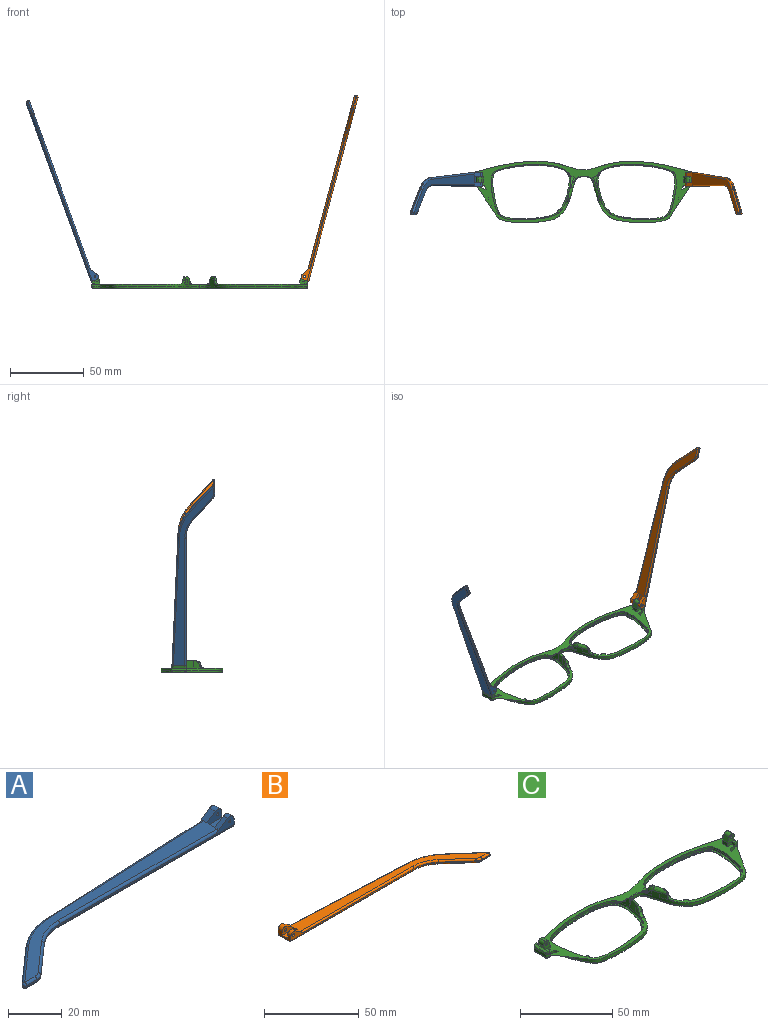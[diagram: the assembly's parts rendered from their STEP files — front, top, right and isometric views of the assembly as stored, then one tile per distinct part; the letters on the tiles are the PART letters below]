
ASSEMBLY  parts=3 mates=2
PART A: 43 faces, bbox 130.2x29.5x5.9 mm
  f0: plane 9.62x3.72mm, normal (1,0,0), area 24.7mm2, adj f1,f3,f4,f5,f10,f16,f18,f28
  f1: cylinder r=2.2mm len=3.45mm, axis (0,-1,0), area 11mm2, adj f0,f2,f4,f37
  f2: plane 6.01x3.91mm, normal (-0.55,0,0.84), area 12.7mm2, adj f1,f4,f9,f19,f37
  f3: plane 2.26x0.1mm, normal (0,0,1), area 0.1mm2, adj f0,f5,f18
  f4: plane 92.1x4.9mm, normal (0,-1,0), area 79.9mm2, adj f0,f1,f2,f14,f19,f36,f42
  f5: plane 93.42x4.13mm, normal (-0.04,1,0), area 64.8mm2, adj f0,f3,f11,f15,f17,f27,f28
  f6: plane 17.82x15.72mm, normal (-0.66,0.75,0), area 14.3mm2, adj f11,f12,f25,f30
  f7: plane 5.46x0.6mm, normal (0,-1,0), area 3.3mm2, adj f12,f13,f23,f32
  f8: plane 14.99x13.23mm, normal (0.66,-0.75,0), area 12mm2, adj f13,f14,f21,f34
  f9: plane 121.18x26.73mm, normal (0,0,1), area 627.7mm2, adj f2,f17,f19,f20,f21,f22,f23,f25
  f10: plane 129.1x27.08mm, normal (0,0,-1), area 686.5mm2, adj f0,f28,f29,f30,f32,f33,f34,f35
  f11: cylinder r=30mm len=18.52mm, axis (0,0,-1), area 12.2mm2, adj f5,f6,f26,f29
  f12: cylinder r=1mm len=1.75mm, axis (0,0,-1), area 1.5mm2, adj f6,f7,f24,f31
  f13: cylinder r=5mm len=3.31mm, axis (0,0,-1), area 2.2mm2, adj f7,f8,f22,f33
  f14: cylinder r=20mm len=13.23mm, axis (0,0,1), area 8.7mm2, adj f4,f8,f20,f35
  f15: plane 5.66x0.25mm, normal (0,0,-1), area 0.7mm2, adj f5,f17,f18
  f16: cylinder r=2.2mm len=3.45mm, axis (0,-1,0), area 14.8mm2, adj f0,f17,f18,f38
  f17: plane 6.01x3.91mm, normal (-0.55,0,0.84), area 16.9mm2, adj f5,f9,f15,f16,f18,f27,f38
  f18: plane 7.92x3.3mm, normal (0,1,0), area 15.9mm2, adj f0,f3,f15,f16,f17,f41
  f19: cylinder r=1mm len=84.18mm, axis (-1,0,0), area 131.4mm2, adj f2,f4,f9,f20
  f20: torus R=21mm, axis (0,0,1), area 23.1mm2, adj f9,f14,f19,f21
  f21: cylinder r=1mm len=15.65mm, axis (-0.75,-0.66,0), area 31.4mm2, adj f8,f9,f20,f22
  f22: torus R=4mm, axis (0,0,1), area 5.3mm2, adj f9,f13,f21,f23
  f23: cylinder r=1mm len=5.46mm, axis (-1,0,0), area 8.6mm2, adj f7,f9,f22,f24
  f24: sphere r=1mm, area 2.4mm2, adj f12,f23,f25
  f25: cylinder r=1mm len=18.48mm, axis (0.75,0.66,0), area 37.3mm2, adj f6,f9,f24,f26
  f26: torus R=29mm, axis (0,0,1), area 31.6mm2, adj f9,f11,f25,f27
  f27: cylinder r=1mm len=85.5mm, axis (1,0.04,0), area 133.5mm2, adj f5,f9,f17,f26
  f28: cylinder r=1mm len=93.46mm, axis (-1,-0.04,0), area 146.9mm2, adj f0,f5,f10,f29
  f29: torus R=29mm, axis (0,0,1), area 31.6mm2, adj f10,f11,f28,f30
  f30: cylinder r=1mm len=18.48mm, axis (-0.75,-0.66,0), area 37.3mm2, adj f6,f10,f29,f31
  f31: sphere r=1mm, area 2.4mm2, adj f12,f30,f32
  f32: cylinder r=1mm len=5.46mm, axis (1,0,0), area 8.6mm2, adj f7,f10,f31,f33
  f33: torus R=4mm, axis (0,0,1), area 5.3mm2, adj f10,f13,f32,f34
  f34: cylinder r=1mm len=15.65mm, axis (0.75,0.66,0), area 31.4mm2, adj f8,f10,f33,f35
  f35: torus R=21mm, axis (0,0,1), area 23.1mm2, adj f10,f14,f34,f36
  f36: cylinder r=1mm len=92.1mm, axis (1,0,0), area 144.7mm2, adj f0,f4,f10,f35
  f37: plane 7.92x4.7mm, normal (0,1,0), area 27mm2, adj f0,f1,f2,f39,f40,f42
  f38: plane 7.92x4.7mm, normal (0,-1,0), area 27mm2, adj f0,f16,f17,f39,f40,f41
  f39: plane 7.92x4.1mm, normal (0,0,1), area 32.5mm2, adj f0,f37,f38,f40
  f40: plane 4.1x1.4mm, normal (1,0,0), area 5.7mm2, adj f9,f37,f38,f39
  f41: cylinder r=0.5mm len=3.1mm, axis (0,-1,0), area 9.7mm2, adj f18,f38
  f42: cylinder r=0.5mm len=2.3mm, axis (0,-1,0), area 7.2mm2, adj f4,f37
PART B: 43 faces, bbox 130.2x29.5x5.9 mm
  f0: plane 9.62x3.72mm, normal (-1,0,0), area 24.7mm2, adj f1,f3,f4,f5,f10,f16,f18,f28
  f1: cylinder r=2.2mm len=3.45mm, axis (0,-1,0), area 11mm2, adj f0,f2,f4,f37
  f2: plane 6.01x3.91mm, normal (0.55,0,0.84), area 12.7mm2, adj f1,f4,f9,f19,f37
  f3: plane 2.26x0.1mm, normal (0,0,1), area 0.1mm2, adj f0,f5,f18
  f4: plane 92.1x4.9mm, normal (0,-1,0), area 78.2mm2, adj f0,f1,f2,f14,f19,f36,f42
  f5: plane 93.42x4.13mm, normal (0.04,1,0), area 64.8mm2, adj f0,f3,f11,f15,f17,f27,f28
  f6: plane 17.82x15.72mm, normal (0.66,0.75,0), area 14.3mm2, adj f11,f12,f25,f30
  f7: plane 5.46x0.6mm, normal (0,-1,0), area 3.3mm2, adj f12,f13,f23,f32
  f8: plane 14.99x13.23mm, normal (-0.66,-0.75,0), area 12mm2, adj f13,f14,f21,f34
  f9: plane 121.18x26.73mm, normal (0,0,1), area 627.7mm2, adj f2,f17,f19,f20,f21,f22,f23,f25
  f10: plane 129.1x27.08mm, normal (0,0,-1), area 686.5mm2, adj f0,f28,f29,f30,f32,f33,f34,f35
  f11: cylinder r=30mm len=18.52mm, axis (0,0,-1), area 12.2mm2, adj f5,f6,f26,f29
  f12: cylinder r=1mm len=1.75mm, axis (0,0,-1), area 1.5mm2, adj f6,f7,f24,f31
  f13: cylinder r=5mm len=3.31mm, axis (0,0,-1), area 2.2mm2, adj f7,f8,f22,f33
  f14: cylinder r=20mm len=13.23mm, axis (0,0,1), area 8.7mm2, adj f4,f8,f20,f35
  f15: plane 5.66x0.25mm, normal (0,0,-1), area 0.7mm2, adj f5,f17,f18
  f16: cylinder r=2.2mm len=3.45mm, axis (0,-1,0), area 14.8mm2, adj f0,f17,f18,f38
  f17: plane 6.01x3.91mm, normal (0.55,0,0.84), area 16.9mm2, adj f5,f9,f15,f16,f18,f27,f38
  f18: plane 7.92x3.3mm, normal (0,1,0), area 14.3mm2, adj f0,f3,f15,f16,f17,f41
  f19: cylinder r=1mm len=84.18mm, axis (1,0,0), area 131.4mm2, adj f2,f4,f9,f20
  f20: torus R=21mm, axis (0,0,1), area 23.1mm2, adj f9,f14,f19,f21
  f21: cylinder r=1mm len=15.65mm, axis (0.75,-0.66,0), area 31.4mm2, adj f8,f9,f20,f22
  f22: torus R=4mm, axis (0,0,1), area 5.3mm2, adj f9,f13,f21,f23
  f23: cylinder r=1mm len=5.46mm, axis (1,0,0), area 8.6mm2, adj f7,f9,f22,f24
  f24: sphere r=1mm, area 2.4mm2, adj f12,f23,f25
  f25: cylinder r=1mm len=18.48mm, axis (-0.75,0.66,0), area 37.3mm2, adj f6,f9,f24,f26
  f26: torus R=29mm, axis (0,0,1), area 31.6mm2, adj f9,f11,f25,f27
  f27: cylinder r=1mm len=85.5mm, axis (-1,0.04,0), area 133.5mm2, adj f5,f9,f17,f26
  f28: cylinder r=1mm len=93.46mm, axis (1,-0.04,0), area 146.9mm2, adj f0,f5,f10,f29
  f29: torus R=29mm, axis (0,0,1), area 31.6mm2, adj f10,f11,f28,f30
  f30: cylinder r=1mm len=18.48mm, axis (0.75,-0.66,0), area 37.3mm2, adj f6,f10,f29,f31
  f31: sphere r=1mm, area 2.4mm2, adj f12,f30,f32
  f32: cylinder r=1mm len=5.46mm, axis (-1,0,0), area 8.6mm2, adj f7,f10,f31,f33
  f33: torus R=4mm, axis (0,0,1), area 5.3mm2, adj f10,f13,f32,f34
  f34: cylinder r=1mm len=15.65mm, axis (-0.75,0.66,0), area 31.4mm2, adj f8,f10,f33,f35
  f35: torus R=21mm, axis (0,0,1), area 23.1mm2, adj f10,f14,f34,f36
  f36: cylinder r=1mm len=92.1mm, axis (-1,0,0), area 144.7mm2, adj f0,f4,f10,f35
  f37: plane 7.92x4.7mm, normal (0,1,0), area 25.4mm2, adj f0,f1,f2,f39,f40,f42
  f38: plane 7.92x4.7mm, normal (0,-1,0), area 25.4mm2, adj f0,f16,f17,f39,f40,f41
  f39: plane 7.92x4.1mm, normal (0,0,1), area 32.5mm2, adj f0,f37,f38,f40
  f40: plane 4.1x1.4mm, normal (-1,0,0), area 5.7mm2, adj f9,f37,f38,f39
  f41: cylinder r=0.88mm len=3.1mm, axis (0,-1,0), area 17mm2, adj f18,f38
  f42: cylinder r=0.88mm len=2.3mm, axis (0,-1,0), area 12.6mm2, adj f4,f37
PART C: 116 faces, bbox 148.1x42.8x10.4 mm
  f0: bspline ~2.65x2.04mm, area 1.9mm2, adj f2,f7,f51,f52,f57
  f1: plane 147.39x42.12mm, normal (0,0,1), area 837.5mm2, adj f4,f5,f6,f7,f8,f12,f20,f23
  f2: bspline ~5.86x5.06mm, area 12.7mm2, adj f0,f7,f37,f42,f44,f51,f52
  f3: plane 4.47x1.44mm, normal (0,0,1), area 0.1mm2, adj f7,f38
  f4: plane 1.23x0.04mm, normal (0,0,1), area 0mm2, adj f1,f7,f22
  f5: plane 6.97x5.07mm, normal (0,1,0), area 22.7mm2, adj f1,f20,f21,f25,f27,f28,f30,f31
  f6: plane 3.2x2.36mm, normal (0,-1,0), area 5.7mm2, adj f1,f20,f26,f29
  f7: extruded ~73.32x41.69mm, area 294.6mm2, adj f0,f1,f2,f3,f4,f8,f13,f14
  f8: extruded ~35.39x5.69mm, area 72.2mm2, adj f1,f7,f18,f66
  f9: plane 144.78x39.72mm, normal (0,0,-1), area 572.2mm2, adj f13,f15,f17,f18,f19,f70,f72,f74
  f10: plane 54.35x37.72mm, normal (0,0,1), area 126.9mm2, adj f11,f19
  f11: extruded ~53.93x37.38mm, area 152.9mm2, adj f10,f12
  f12: extruded ~53.93x37.38mm, area 173.4mm2, adj f1,f11,f39,f40,f41,f42,f44,f45
  f13: bspline ~73.12x32.25mm, area 165.1mm2, adj f7,f9,f14,f70
  f14: bspline ~1x1mm, area 0.8mm2, adj f7,f13,f15
  f15: bspline ~8.63x1.2mm, area 12.6mm2, adj f7,f9,f14,f16
  f16: bspline ~1.04x1mm, area 0.7mm2, adj f7,f15,f17
  f17: bspline ~45.7x8.55mm, area 59.8mm2, adj f7,f9,f16,f18
  f18: bspline ~37.17x6.7mm, area 56.6mm2, adj f8,f9,f17,f75
  f19: bspline ~53.98x38.33mm, area 237.8mm2, adj f9,f10
  f20: plane 4x2.36mm, normal (-1,0,0), area 9.5mm2, adj f1,f5,f6,f21
  f21: plane 4x0.02mm, normal (0.34,0,0.94), area 0.1mm2, adj f5,f20,f28
  f22: plane 2.76x2.53mm, normal (0,-1,0), area 3.9mm2, adj f4,f26,f27,f35,f55
  f23: plane 7.67x1.6mm, normal (0.94,0,-0.34), area 13mm2, adj f1,f35,f36,f55
  f24: plane 2.1x1.69mm, normal (0,1,0), area 2.8mm2, adj f1,f25,f27,f36,f55
  f25: plane 3.3x2.1mm, normal (-1,0,0), area 6.9mm2, adj f1,f5,f24,f27
  f26: plane 2.35x2.1mm, normal (-1,0,0), area 4.9mm2, adj f1,f6,f22,f27,f29
  f27: plane 9.65x1.24mm, normal (0,0,1), area 8.2mm2, adj f5,f22,f24,f25,f26,f29,f30,f55
  f28: plane 4x3.31mm, normal (-0.94,0,0.34), area 14.1mm2, adj f5,f21,f29,f32
  f29: plane 5.77x5.06mm, normal (0,-1,0), area 17mm2, adj f6,f26,f27,f28,f30,f31,f32,f33
  f30: plane 4x2.21mm, normal (0.94,0,-0.34), area 9.4mm2, adj f5,f27,f29,f33
  f31: plane 4x0.01mm, normal (0.34,0,0.94), area 0mm2, adj f5,f29,f32,f33
  f32: cylinder r=1.98mm len=4mm, axis (0,1,0), area 12.4mm2, adj f5,f28,f29,f31
  f33: cylinder r=1.98mm len=4mm, axis (0,-1,0), area 12.4mm2, adj f5,f29,f30,f31
  f34: cylinder r=0.88mm len=4mm, axis (0,-1,0), area 22mm2, adj f5,f29
  f35: cone r=1mm half-angle=20deg, axis (0,0,1), area 2.3mm2, adj f1,f22,f23,f55
  f36: cylinder r=1mm len=2.28mm, axis (-0.34,0,-0.94), area 3mm2, adj f1,f23,f24,f55
  f37: extruded ~3.67x3.11mm, area 5.9mm2, adj f2,f7,f51,f58
  f38: extruded ~4.44x3.34mm, area 15.2mm2, adj f3,f7,f43,f44,f54
  f39: extruded ~6.76x5mm, area 19.1mm2, adj f1,f12,f43,f44,f54
  f40: extruded ~4.98x0.54mm, area 2.7mm2, adj f12,f42
  f41: plane 3.69x0.99mm, normal (0,0,1), area 0.3mm2, adj f12,f42,f44
  f42: bspline ~8.14x4.16mm, area 6.4mm2, adj f2,f12,f40,f41,f53
  f43: bspline ~7.26x7.26mm, area 6.3mm2, adj f38,f39,f44,f54
  f44: bspline ~10.48x4.89mm, area 22.2mm2, adj f2,f7,f12,f38,f39,f41,f43
  f45: plane 2.74x1.51mm, normal (0,0,-1), area 1.7mm2, adj f12,f46
  f46: cylinder r=2.28mm len=2.71mm, axis (0,0,1), area 1.7mm2, adj f1,f12,f45,f53
  f47: plane 2.37x2.28mm, normal (0,0,-1), area 3.1mm2, adj f12,f48
  f48: cylinder r=1.3mm len=2.36mm, axis (0,0,1), area 2.2mm2, adj f1,f12,f47
  f49: plane 2.41x1.67mm, normal (0,0,-1), area 2.2mm2, adj f12,f50
  f50: cylinder r=1.3mm len=2.4mm, axis (0,0,1), area 1.9mm2, adj f1,f12,f49
  f51: bspline ~1.73x1.17mm, area 0.7mm2, adj f0,f2,f7,f37
  f52: bspline ~3.55x3.47mm, area 3.7mm2, adj f0,f1,f2,f53,f57
  f53: bspline ~6.16x4.45mm, area 7.6mm2, adj f1,f12,f42,f46,f52
  f54: bspline ~3.78x3.75mm, area 7.1mm2, adj f1,f7,f38,f39,f43
  f55: plane 9.71x1.44mm, normal (0.34,0,0.94), area 13.9mm2, adj f22,f23,f24,f27,f35,f36
  f56: bspline ~6.39x2.13mm, area 2.6mm2, adj f1,f7,f57,f113
  f57: bspline ~2.1x1.46mm, area 0.6mm2, adj f0,f7,f52,f56
  f58: bspline ~5.25x1.75mm, area 0mm2, adj f7,f37
  f59: bspline ~2.65x2.03mm, area 1.9mm2, adj f60,f65,f108,f109,f114
  f60: bspline ~5.86x5.06mm, area 12.6mm2, adj f59,f65,f94,f99,f101,f108,f109
  f61: plane 4.47x1.44mm, normal (0,0,1), area 0.1mm2, adj f65,f95
  f62: plane 1.23x0.04mm, normal (0,0,1), area 0mm2, adj f1,f65,f79
  f63: plane 6.97x5.07mm, normal (0,1,0), area 22.7mm2, adj f1,f77,f78,f82,f84,f85,f87,f88
  f64: plane 3.2x2.36mm, normal (0,-1,0), area 5.7mm2, adj f1,f77,f83,f86
  f65: extruded ~73.32x41.69mm, area 294.6mm2, adj f1,f7,f59,f60,f61,f62,f66,f70
  f66: extruded ~35.39x5.69mm, area 72.2mm2, adj f1,f8,f65,f75
  f67: plane 54.35x37.72mm, normal (0,0,1), area 126.9mm2, adj f68,f76
  f68: extruded ~53.93x37.38mm, area 152.9mm2, adj f67,f69
  f69: extruded ~53.93x37.38mm, area 173.4mm2, adj f1,f68,f96,f97,f98,f99,f101,f102
  f70: bspline ~72.96x32.25mm, area 165.1mm2, adj f9,f13,f65,f71
  f71: bspline ~1x1mm, area 0.8mm2, adj f65,f70,f72
  f72: bspline ~8.63x1.2mm, area 12.6mm2, adj f9,f65,f71,f73
  f73: bspline ~1.04x1mm, area 0.7mm2, adj f65,f72,f74
  f74: bspline ~45.7x8.55mm, area 59.8mm2, adj f9,f65,f73,f75
  f75: bspline ~37.17x6.7mm, area 56.6mm2, adj f9,f18,f66,f74
  f76: bspline ~53.98x38.33mm, area 237.8mm2, adj f9,f67
  f77: plane 4x2.36mm, normal (1,0,0), area 9.5mm2, adj f1,f63,f64,f78
  f78: plane 4x0.02mm, normal (-0.34,0,0.94), area 0.1mm2, adj f63,f77,f85
  f79: plane 2.76x2.53mm, normal (0,-1,0), area 3.9mm2, adj f62,f83,f84,f92,f112
  f80: plane 7.67x1.6mm, normal (-0.94,0,-0.34), area 13mm2, adj f1,f92,f93,f112
  f81: plane 2.1x1.69mm, normal (0,1,0), area 2.8mm2, adj f1,f82,f84,f93,f112
  f82: plane 3.3x2.1mm, normal (1,0,0), area 6.9mm2, adj f1,f63,f81,f84
  f83: plane 2.35x2.1mm, normal (1,0,0), area 4.9mm2, adj f1,f64,f79,f84,f86
  f84: plane 9.65x1.24mm, normal (0,0,1), area 8.2mm2, adj f63,f79,f81,f82,f83,f86,f87,f112
  f85: plane 4x3.31mm, normal (0.94,0,0.34), area 14.1mm2, adj f63,f78,f86,f89
  f86: plane 5.77x5.06mm, normal (0,-1,0), area 17mm2, adj f64,f83,f84,f85,f87,f88,f89,f90
  f87: plane 4x2.21mm, normal (-0.94,0,-0.34), area 9.4mm2, adj f63,f84,f86,f90
  f88: plane 4x0.01mm, normal (-0.34,0,0.94), area 0mm2, adj f63,f86,f89,f90
  f89: cylinder r=1.98mm len=4mm, axis (0,1,0), area 12.4mm2, adj f63,f85,f86,f88
  f90: cylinder r=1.98mm len=4mm, axis (0,-1,0), area 12.4mm2, adj f63,f86,f87,f88
  f91: cylinder r=0.88mm len=4mm, axis (0,-1,0), area 22mm2, adj f63,f86
  f92: cone r=1mm half-angle=20deg, axis (0,0,1), area 2.3mm2, adj f1,f79,f80,f112
  f93: cylinder r=1mm len=2.28mm, axis (0.34,0,-0.94), area 3mm2, adj f1,f80,f81,f112
  f94: extruded ~3.67x3.11mm, area 5.9mm2, adj f60,f65,f108,f115
  f95: extruded ~4.44x3.34mm, area 15.2mm2, adj f61,f65,f100,f101,f111
  f96: extruded ~6.76x5mm, area 19.1mm2, adj f1,f69,f100,f101,f111
  f97: extruded ~4.98x0.54mm, area 2.7mm2, adj f69,f99
  f98: plane 3.69x0.99mm, normal (0,0,1), area 0.3mm2, adj f69,f99,f101
  f99: bspline ~8.14x4.16mm, area 6.4mm2, adj f60,f69,f97,f98,f110
  f100: bspline ~7.26x7.26mm, area 6.2mm2, adj f95,f96,f101,f111
  f101: bspline ~10.85x5.02mm, area 22.4mm2, adj f60,f65,f69,f95,f96,f98,f100
  f102: plane 2.74x1.51mm, normal (0,0,-1), area 1.7mm2, adj f69,f103
  f103: cylinder r=2.28mm len=2.71mm, axis (0,0,1), area 1.7mm2, adj f1,f69,f102,f110
  f104: plane 2.37x2.28mm, normal (0,0,-1), area 3.1mm2, adj f69,f105
  f105: cylinder r=1.3mm len=2.36mm, axis (0,0,1), area 2.2mm2, adj f1,f69,f104
  f106: plane 2.41x1.67mm, normal (0,0,-1), area 2.2mm2, adj f69,f107
  f107: cylinder r=1.3mm len=2.4mm, axis (0,0,1), area 1.9mm2, adj f1,f69,f106
  f108: bspline ~2.14x1.35mm, area 0.7mm2, adj f59,f60,f65,f94
  f109: bspline ~3.55x3.47mm, area 3.7mm2, adj f1,f59,f60,f110,f114
  f110: bspline ~5.94x4.42mm, area 7.6mm2, adj f1,f69,f99,f103,f109
  f111: bspline ~3.78x3.75mm, area 7.1mm2, adj f1,f65,f95,f96,f100
  f112: plane 9.71x1.44mm, normal (-0.34,0,0.94), area 13.9mm2, adj f79,f80,f81,f84,f92,f93
  f113: bspline ~6.39x2.13mm, area 2.6mm2, adj f1,f56,f65,f114
  f114: bspline ~2.1x1.46mm, area 0.6mm2, adj f59,f65,f109,f113
  f115: bspline ~5.25x1.75mm, area 0mm2, adj f65,f94
PLACE A rot(axis=(0,1,0),70deg) t=(-84.77,-5.75,56)mm
PLACE B rot(axis=(0,-1,0),75deg) t=(68.2,-5.75,-61.61)mm
PLACE C t=(10.15,-1.13,-5.77)mm
MATE revolute A.f1 <-> C.f89  axis (0,-1,0) through (-60.89,2.72,1.22)mm
MATE revolute B.f41 <-> C.f33  axis (0,-1,0) through (81.2,2.72,1.21)mm
